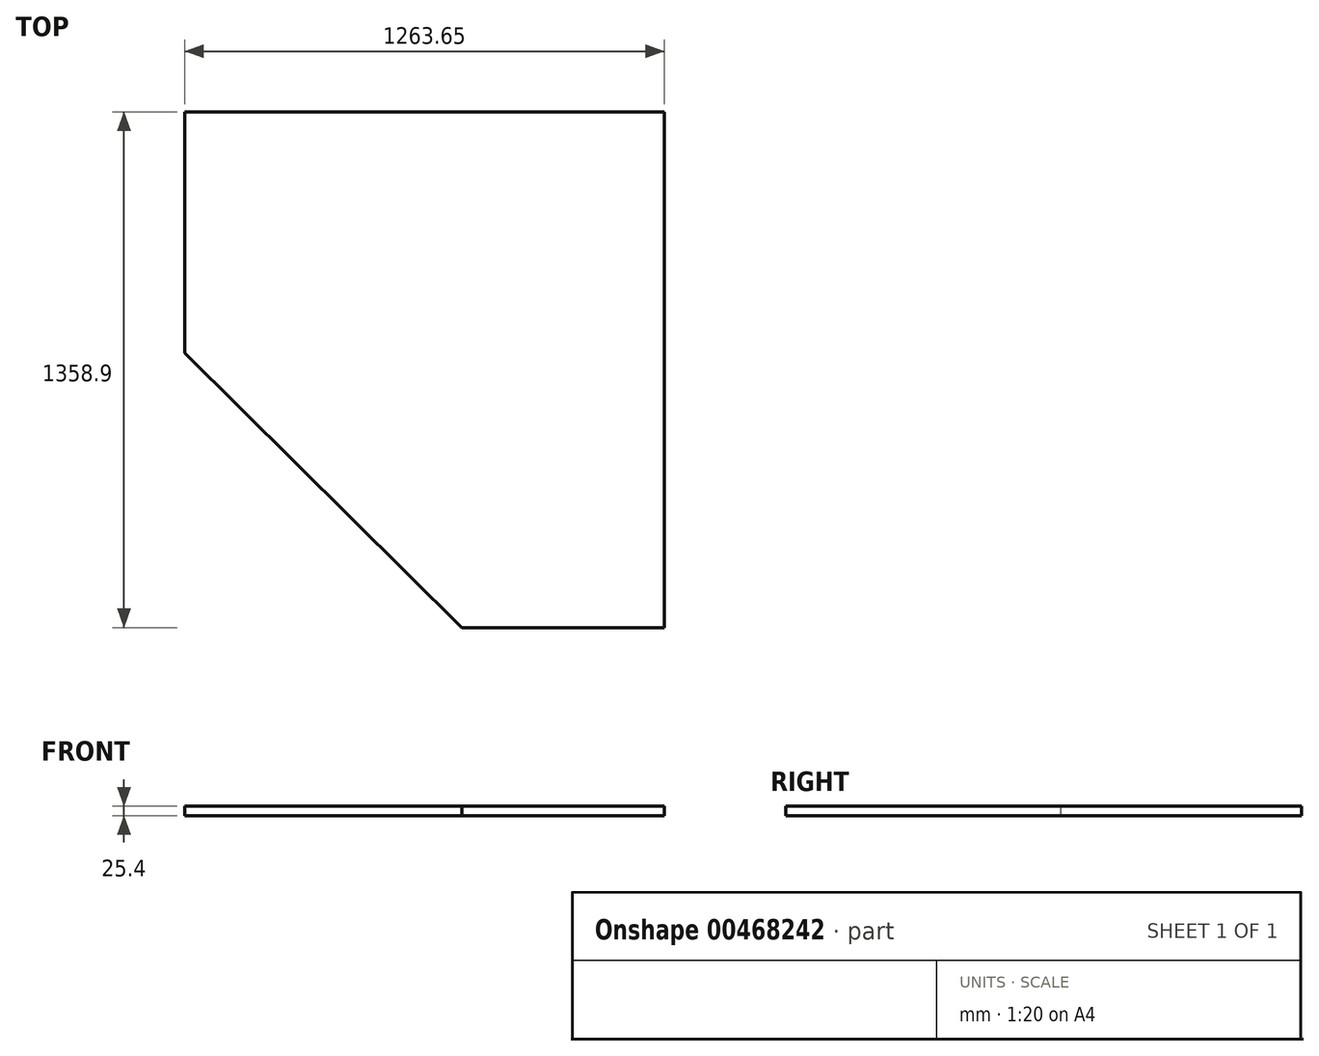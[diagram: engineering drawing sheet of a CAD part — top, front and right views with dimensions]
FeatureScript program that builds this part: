
annotation { "Feature Type Name" : "Feature", "Feature Type Description" : "" }
export const myFeature = defineFeature(function(context is Context, id is Id, definition is map)
    precondition{}
    {
        {
            var Q0;
            Q0=qCreatedBy(makeId("Top.planeOp"),FACE);
            var sketch = newSketch(context, id + "F0", { "sketchPlane" : qUnion([Q0])});
            skLineSegment(sketch, "E0", {"start": v(0, 0) * mm, "end": v(-1263.65, 0) * mm});
            skLineSegment(sketch, "E1", {"start": v(-1263.65, 0) * mm, "end": v(-1263.65, -635) * mm});
            skLineSegment(sketch, "E2", {"start": v(-1263.65, -635) * mm, "end": v(-533.4, -1358.9) * mm});
            skLineSegment(sketch, "E3", {"start": v(-533.4, -1358.9) * mm, "end": v(0, -1358.9) * mm});
            skLineSegment(sketch, "E4", {"start": v(0, -1358.9) * mm, "end": v(0, 0) * mm});
            skSolve(sketch);
        }
        {
            var Q0;
            Q0=qSketchRegion(id+"F0",true);
            extrude(context, id + "F1", {"entities" : qUnion([Q0]), "depth" : 25.4 * mm});
        }
    });
